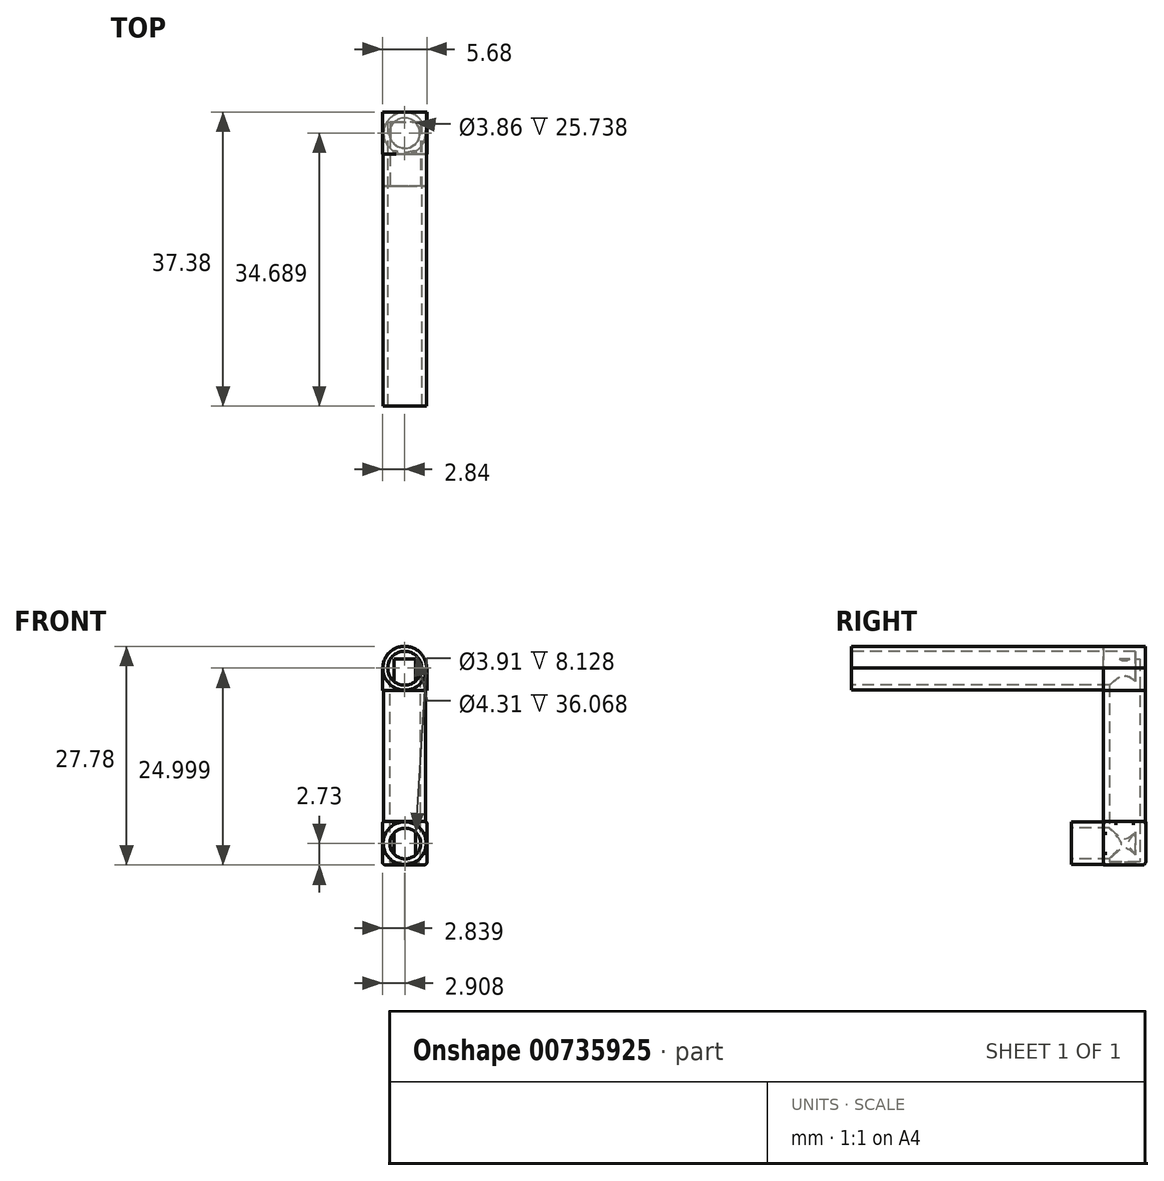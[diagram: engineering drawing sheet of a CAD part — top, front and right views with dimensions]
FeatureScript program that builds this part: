
annotation { "Feature Type Name" : "Feature", "Feature Type Description" : "" }
export const myFeature = defineFeature(function(context is Context, id is Id, definition is map)
    precondition{}
    {
        {
            var Q0;
            Q0=qCreatedBy(makeId("Front.planeOp"),FACE);
            var sketch = newSketch(context, id + "F0", { "sketchPlane" : qUnion([Q0])});
            skCircle(sketch, "E0", {"center": v(-56.37, 14.7) * mm, "radius": 2.78 * mm});
            skSolve(sketch);
        }
        {
            var Q0;
            Q0 = qSketchRegion(id + "F0", true);
            extrude(context, id + "F1", {"entities" : qUnion([Q0]), "depth" : 32 * mm, "offsetDistance" : 25.4 * mm});
        }
        {
            var Q0;
            Q0=makeQuery(id+"F1.opExtrude","CAP_FACE",FACE,{"disambiguationData":[OSD([sQuery(id+"F0.wireOp",EDGE,"E0")])],"isStart":true});
            var sketch = newSketch(context, id + "F2", { "sketchPlane" : qUnion([Q0])});
            skLineSegment(sketch, "E1.bottom", {"start": v(53.55, 11.9) * mm, "end": v(59.2, 11.9) * mm});
            skLineSegment(sketch, "E1.top", {"start": v(53.55, 17.5) * mm, "end": v(59.2, 17.5) * mm});
            skLineSegment(sketch, "E1.left", {"start": v(53.55, 11.9) * mm, "end": v(53.55, 17.5) * mm});
            skLineSegment(sketch, "E1.right", {"start": v(59.2, 11.9) * mm, "end": v(59.2, 17.5) * mm});
            skSolve(sketch);
        }
        {
            var Q0;
            Q0 = qSketchRegion(id + "F2", true);
            extrude(context, id + "F3", {"entities" : qUnion([Q0]), "operationType" : NewBodyOperationType.ADD, "depth" : 5.33 * mm, "offsetDistance" : 25.4 * mm});
        }
        {
            var Q0;
            Q0=makeQuery(id+"F3.opExtrude","CAP_FACE",FACE,{"disambiguationData":[OSD([sQuery(id+"F2.wireOp",EDGE,"E1.bottom"),sQuery(id+"F2.wireOp",EDGE,"E1.top"),sQuery(id+"F2.wireOp",EDGE,"E1.left"),sQuery(id+"F2.wireOp",EDGE,"E1.right")])],"isStart":false});
            var sketch = newSketch(context, id + "F4", { "sketchPlane" : qUnion([Q0])});
            skCircle(sketch, "E2", {"center": v(56.38, 14.7) * mm, "radius": 2.78 * mm});
            skPoint(sketch, "E2.centerSnap0", {"position": v(56.38, 17.5) * mm});
            skPoint(sketch, "E2.centerSnap1", {"position": v(53.55, 14.7) * mm});
            skLineSegment(sketch, "E3", {"start": v(53.55, 14.7) * mm, "end": v(52.3, 14.94) * mm});
            skLineSegment(sketch, "E4", {"start": v(52.3, 14.94) * mm, "end": v(52.23, 18.66) * mm});
            skLineSegment(sketch, "E5", {"start": v(52.23, 18.66) * mm, "end": v(58.17, 18.32) * mm});
            skLineSegment(sketch, "E6", {"start": v(58.17, 18.32) * mm, "end": v(60.2, 18.18) * mm});
            skLineSegment(sketch, "E7", {"start": v(60.2, 18.18) * mm, "end": v(60.02, 15.4) * mm});
            skLineSegment(sketch, "E8", {"start": v(60.02, 15.4) * mm, "end": v(59.2, 14.7) * mm});
            skLineSegment(sketch, "E9", {"start": v(53.55, 14.7) * mm, "end": v(53.6, 14.7) * mm});
            skLineSegment(sketch, "E10", {"start": v(59.2, 14.7) * mm, "end": v(59.16, 14.7) * mm});
            skSolve(sketch);
        }
        {
            var Q0;
            {var subQ3=sQuery(id+"F4.wireOp",EDGE,"E3");Q0=makeQuery(id+"F4.imprint","IMPRINT",FACE,{"disambiguationData":[TD([[makeQuery(id+"F4.imprint","IMPRINT",EDGE,{"derivedFrom":subQ3}),-1.0]])]});}
            var Q1;
            {var subQ1=sQuery(id+"F4.wireOp",EDGE,"E9");Q1=makeQuery(id+"F4.imprint","IMPRINT",FACE,{"disambiguationData":[TD([[makeQuery(id+"F4.imprint","IMPRINT",EDGE,{"derivedFrom":subQ1}),1.0]])]});}
            extrude(context, id + "F5", {"entities" : qUnion([Q0, Q1]), "operationType" : NewBodyOperationType.REMOVE, "oppositeDirection" : true, "depth" : 43.18 * mm, "offsetDistance" : 25.4 * mm});
        }
        {
            var Q0;
            Q0=makeQuery(id+"F3.opExtrude","SWEPT_FACE",FACE,{"disambiguationData":[OSD([sQuery(id+"F2.wireOp",EDGE,"E1.bottom")])]});
            var sketch = newSketch(context, id + "F6", { "sketchPlane" : qUnion([Q0])});
            skCircle(sketch, "E11", {"center": v(-56.38, -2.67) * mm, "radius": 2.66 * mm});
            skPoint(sketch, "E11.centerSnap0", {"position": v(-53.55, -2.67) * mm});
            skPoint(sketch, "E11.centerSnap1", {"position": v(-56.38, -5.33) * mm});
            skSolve(sketch);
        }
        {
            var Q0;
            Q0 = qSketchRegion(id + "F6", true);
            extrude(context, id + "F7", {"entities" : qUnion([Q0]), "operationType" : NewBodyOperationType.ADD, "depth" : 16.66 * mm, "offsetDistance" : 25.4 * mm});
        }
        {
            var Q0;
            Q0=makeQuery(id+"F7.opExtrude","CAP_FACE",FACE,{"disambiguationData":[OSD([sQuery(id+"F6.wireOp",EDGE,"E11")])],"isStart":false});
            var sketch = newSketch(context, id + "F8", { "sketchPlane" : qUnion([Q0])});
            skLineSegment(sketch, "E12.bottom", {"start": v(-53.53, -5.38) * mm, "end": v(-59.2, -5.38) * mm});
            skLineSegment(sketch, "E12.top", {"start": v(-53.53, 0) * mm, "end": v(-59.2, 0) * mm});
            skLineSegment(sketch, "E12.left", {"start": v(-53.53, -5.38) * mm, "end": v(-53.53, 0) * mm});
            skLineSegment(sketch, "E12.right", {"start": v(-59.2, -5.38) * mm, "end": v(-59.2, 0) * mm});
            skSolve(sketch);
        }
        {
            var Q0;
            Q0 = qSketchRegion(id + "F8", true);
            extrude(context, id + "F9", {"entities" : qUnion([Q0]), "operationType" : NewBodyOperationType.ADD, "depth" : 5.54 * mm, "offsetDistance" : 25.4 * mm});
        }
        {
            var Q0;
            Q0=makeQuery(id+"F9.opExtrude","SWEPT_FACE",FACE,{"disambiguationData":[OSD([sQuery(id+"F8.wireOp",EDGE,"E12.top")])]});
            var sketch = newSketch(context, id + "F10", { "sketchPlane" : qUnion([Q0])});
            skCircle(sketch, "E13", {"center": v(-56.37, -7.53) * mm, "radius": 2.72 * mm});
            skPoint(sketch, "E13.centerSnap0", {"position": v(-53.53, -7.53) * mm});
            skPoint(sketch, "E13.centerSnap1", {"position": v(-56.37, -10.3) * mm});
            skSolve(sketch);
        }
        {
            var Q0;
            Q0 = qSketchRegion(id + "F10", true);
            extrude(context, id + "F11", {"entities" : qUnion([Q0]), "operationType" : NewBodyOperationType.ADD, "depth" : 4.06 * mm, "offsetDistance" : 25.4 * mm});
        }
        {
            var Q0;
            Q0=makeQuery(id+"F9.opExtrude","SWEPT_EDGE",EDGE,{"disambiguationData":[OSD([sQuery(id+"F8.wireOp",EDGE,"E12.top"),sQuery(id+"F8.wireOp",EDGE,"E12.left")])]});
            var Q1;
            Q1=makeQuery(id+"F9.opExtrude","CAP_EDGE",EDGE,{"disambiguationData":[OSD([sQuery(id+"F8.wireOp",EDGE,"E12.left")])],"isStart":false});
            var Q2;
            Q2=makeQuery(id+"F9.opExtrude","SWEPT_EDGE",EDGE,{"disambiguationData":[OSD([sQuery(id+"F8.wireOp",EDGE,"E12.bottom"),sQuery(id+"F8.wireOp",EDGE,"E12.left")])]});
            var Q3;
            Q3=makeQuery(id+"F9.opExtrude","CAP_EDGE",EDGE,{"disambiguationData":[OSD([sQuery(id+"F8.wireOp",EDGE,"E12.bottom")])],"isStart":false});
            var Q4;
            Q4=makeQuery(id+"F9.opExtrude","CAP_EDGE",EDGE,{"disambiguationData":[OSD([sQuery(id+"F8.wireOp",EDGE,"E12.top")])],"isStart":false});
            var Q5;
            Q5=makeQuery(id+"F9.opExtrude","CAP_EDGE",EDGE,{"disambiguationData":[OSD([sQuery(id+"F8.wireOp",EDGE,"E12.right")])],"isStart":false});
            var Q6;
            Q6=makeQuery(id+"F9.opExtrude","SWEPT_EDGE",EDGE,{"disambiguationData":[OSD([sQuery(id+"F8.wireOp",EDGE,"E12.top"),sQuery(id+"F8.wireOp",EDGE,"E12.right")])]});
            var Q7;
            Q7=makeQuery(id+"F9.opExtrude","CAP_EDGE",EDGE,{"disambiguationData":[OSD([sQuery(id+"F8.wireOp",EDGE,"E12.right")])],"isStart":true});
            var Q8;
            Q8=makeQuery(id+"F9.opExtrude","CAP_EDGE",EDGE,{"disambiguationData":[OSD([sQuery(id+"F8.wireOp",EDGE,"E12.left")])],"isStart":true});
            var Q9;
            Q9=makeQuery(id+"F9.opExtrude","CAP_EDGE",EDGE,{"disambiguationData":[OSD([sQuery(id+"F8.wireOp",EDGE,"E12.bottom")])],"isStart":true});
            var Q10;
            Q10=makeQuery(id+"F9.opExtrude","SWEPT_EDGE",EDGE,{"disambiguationData":[OSD([sQuery(id+"F8.wireOp",EDGE,"E12.bottom"),sQuery(id+"F8.wireOp",EDGE,"E12.right")])]});
            var Q11;
            {var subQ0=sQuery(id+"F8.wireOp",EDGE,"E12.right");var subQ1=sQuery(id+"F8.wireOp",EDGE,"E12.top");Q11=makeQuery(id+"F9.boolean.opBoolean","SPLIT",EDGE,{"disambiguationData":[TD([makeQuery(id+"F9.opExtrude","SWEPT_FACE",FACE,{"disambiguationData":[OSD([subQ0])]})])],"derivedFrom":makeQuery(id+"F9.opExtrude","CAP_EDGE",EDGE,{"disambiguationData":[OSD([subQ1])],"isStart":true})});}
            var Q12;
            {var subQ0=sQuery(id+"F8.wireOp",EDGE,"E12.left");var subQ1=sQuery(id+"F8.wireOp",EDGE,"E12.top");Q12=makeQuery(id+"F9.boolean.opBoolean","SPLIT",EDGE,{"disambiguationData":[TD([makeQuery(id+"F9.opExtrude","SWEPT_FACE",FACE,{"disambiguationData":[OSD([subQ0])]})])],"derivedFrom":makeQuery(id+"F9.opExtrude","CAP_EDGE",EDGE,{"disambiguationData":[OSD([subQ1])],"isStart":true})});}
            fillet(context, id + "F12", {"entities" : qUnion([Q0, Q1, Q2, Q3, Q4, Q5, Q6, Q7, Q8, Q9, Q10, Q11, Q12]), "radius" : 0.43 * mm, "tangentPropagation" : true, "allowEdgeOverflow" : false});
        }
        {
            var Q0;
            Q0=makeQuery(id+"F1.opExtrude","CAP_FACE",FACE,{"disambiguationData":[OSD([sQuery(id+"F0.wireOp",EDGE,"E0")])],"isStart":false});
            var sketch = newSketch(context, id + "F13", { "sketchPlane" : qUnion([Q0])});
            skCircle(sketch, "E14", {"center": v(-56.37, 14.7) * mm, "radius": 2.15 * mm});
            skCircle(sketch, "E15", {"center": v(-56.3, -7.57) * mm, "radius": 1.95 * mm});
            skSolve(sketch);
        }
        {
            var Q0;
            Q0 = qSketchRegion(id + "F13", true);
            extrude(context, id + "F14", {"entities" : qUnion([Q0]), "operationType" : NewBodyOperationType.REMOVE, "oppositeDirection" : true, "depth" : 36.07 * mm, "offsetDistance" : 25.4 * mm});
        }
        {
            var Q0;
            Q0=makeQuery(id+"F9.opExtrude","CAP_FACE",FACE,{"disambiguationData":[OSD([sQuery(id+"F8.wireOp",EDGE,"E12.bottom"),sQuery(id+"F8.wireOp",EDGE,"E12.top"),sQuery(id+"F8.wireOp",EDGE,"E12.left"),sQuery(id+"F8.wireOp",EDGE,"E12.right")])],"isStart":false});
            var sketch = newSketch(context, id + "F15", { "sketchPlane" : qUnion([Q0])});
            skCircle(sketch, "E16", {"center": v(-56.37, -2.69) * mm, "radius": 1.93 * mm});
            skPoint(sketch, "E16.centerSnap0", {"position": v(-53.96, -2.69) * mm});
            skPoint(sketch, "E16.centerSnap1", {"position": v(-56.37, -4.95) * mm});
            skSolve(sketch);
        }
        {
            var Q0;
            Q0 = qSketchRegion(id + "F15", true);
            extrude(context, id + "F16", {"entities" : qUnion([Q0]), "operationType" : NewBodyOperationType.REMOVE, "oppositeDirection" : true, "depth" : 26.16 * mm, "offsetDistance" : 25.4 * mm});
        }
        {
            var Q0;
            Q0=makeQuery(id+"F9.opExtrude","CAP_FACE",FACE,{"disambiguationData":[OSD([sQuery(id+"F8.wireOp",EDGE,"E12.bottom"),sQuery(id+"F8.wireOp",EDGE,"E12.top"),sQuery(id+"F8.wireOp",EDGE,"E12.left"),sQuery(id+"F8.wireOp",EDGE,"E12.right")])],"isStart":false});
            var sketch = newSketch(context, id + "F17", { "sketchPlane" : qUnion([Q0])});
            skLineSegment(sketch, "E17.bottom", {"start": v(-53.96, -4.95) * mm, "end": v(-58.78, -4.95) * mm});
            skLineSegment(sketch, "E17.top", {"start": v(-53.96, -0.43) * mm, "end": v(-58.78, -0.43) * mm});
            skLineSegment(sketch, "E17.left", {"start": v(-53.96, -4.95) * mm, "end": v(-53.96, -0.43) * mm});
            skLineSegment(sketch, "E17.right", {"start": v(-58.78, -4.95) * mm, "end": v(-58.78, -0.43) * mm});
            skSolve(sketch);
        }
        {
            var Q0;
            Q0 = qSketchRegion(id + "F17", true);
            extrude(context, id + "F18", {"entities" : qUnion([Q0]), "operationType" : NewBodyOperationType.ADD, "oppositeDirection" : true, "depth" : 0.42 * mm, "offsetDistance" : 25.4 * mm});
        }
    });
